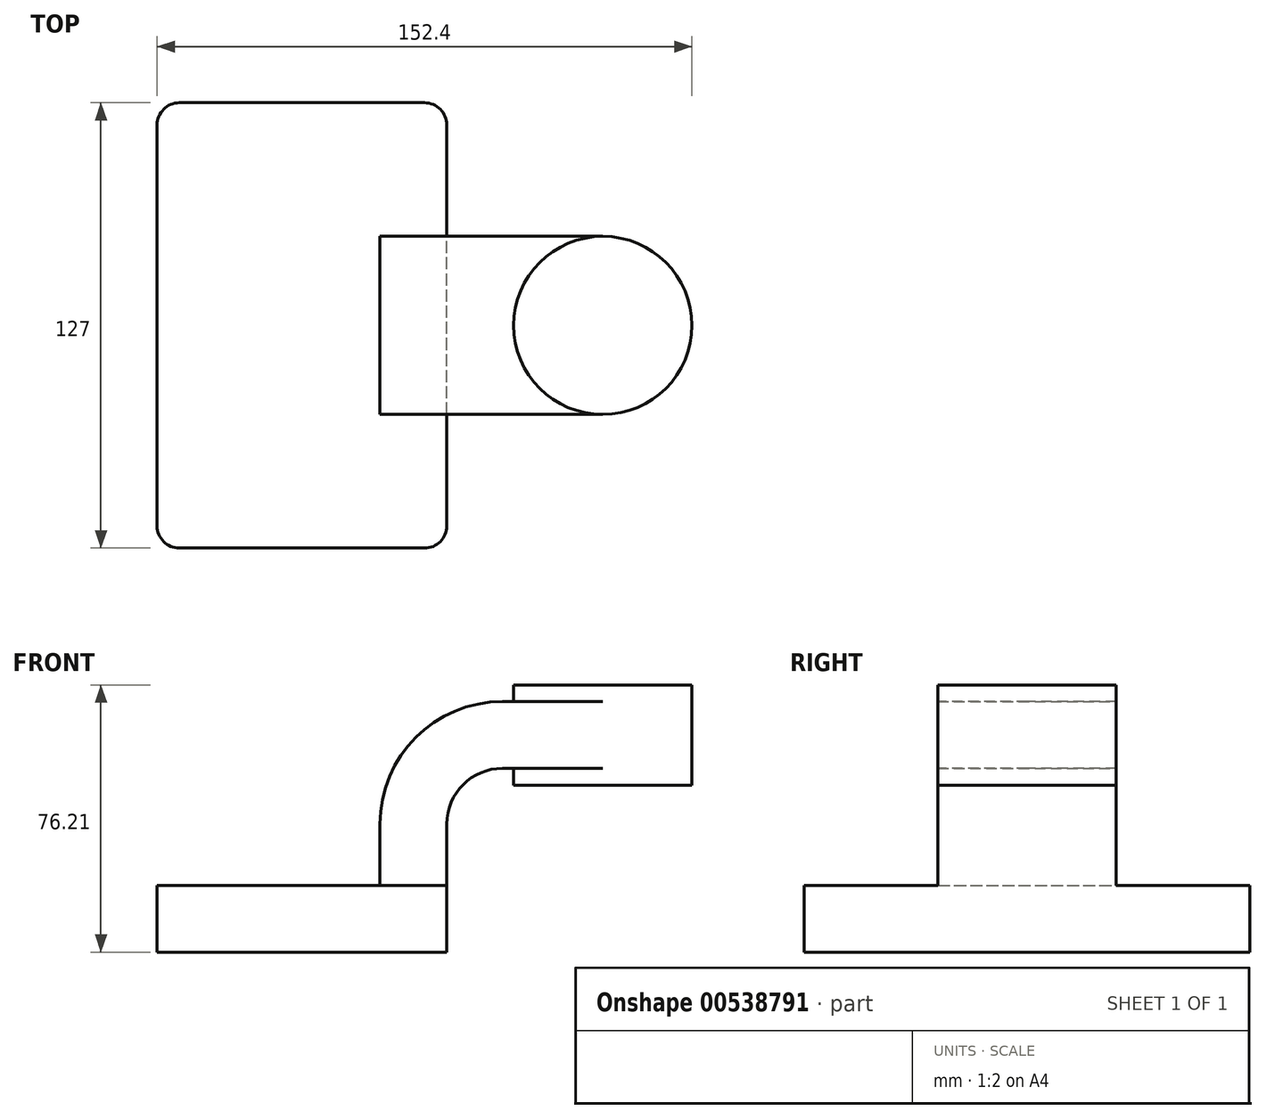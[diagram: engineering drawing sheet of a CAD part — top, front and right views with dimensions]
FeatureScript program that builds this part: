
annotation { "Feature Type Name" : "Feature", "Feature Type Description" : "" }
export const myFeature = defineFeature(function(context is Context, id is Id, definition is map)
    precondition{}
    {
        {
            var Q0;
            Q0=qCreatedBy(makeId("Front.planeOp"),FACE);
            var sketch = newSketch(context, id + "F0", { "sketchPlane" : qUnion([Q0])});
            skLineSegment(sketch, "E0.bottom", {"start": v(-41.27, -9.53) * mm, "end": v(41.28, -9.53) * mm});
            skLineSegment(sketch, "E0.top", {"start": v(-41.28, 9.53) * mm, "end": v(41.28, 9.53) * mm});
            skLineSegment(sketch, "E0.left", {"start": v(-41.28, -9.53) * mm, "end": v(-41.28, 9.53) * mm});
            skLineSegment(sketch, "E0.right", {"start": v(41.28, -9.53) * mm, "end": v(41.28, 9.53) * mm});
            skPoint(sketch, "E0.middle", {"position": v(0, 0) * mm});
            skLineSegment(sketch, "E1.bottom", {"start": v(60.32, 38.1) * mm, "end": v(111.12, 38.1) * mm});
            skLineSegment(sketch, "E1.top", {"start": v(60.32, 66.67) * mm, "end": v(111.12, 66.67) * mm});
            skLineSegment(sketch, "E1.left", {"start": v(60.32, 38.1) * mm, "end": v(60.32, 66.67) * mm});
            skLineSegment(sketch, "E1.right", {"start": v(111.12, 38.1) * mm, "end": v(111.12, 66.67) * mm});
            skPoint(sketch, "E1.middle", {"position": v(85.72, 52.39) * mm});
            skLineSegment(sketch, "E2", {"start": v(41.28, 9.53) * mm, "end": v(41.28, 27) * mm});
            skArc(sketch, "E3", {"start": v(41.27, 27) * mm, "mid": v(45.92, 38.23) * mm, "end": v(57.15, 42.88) * mm});
            skLineSegment(sketch, "E4", {"start": v(57.15, 42.88) * mm, "end": v(85.72, 42.88) * mm});
            skLineSegment(sketch, "E5.0", {"start": v(57.15, 61.93) * mm, "end": v(85.72, 61.93) * mm});
            skArc(sketch, "E5.1", {"start": v(22.23, 27) * mm, "mid": v(32.45, 51.7) * mm, "end": v(57.15, 61.93) * mm});
            skLineSegment(sketch, "E5.2", {"start": v(22.22, 9.53) * mm, "end": v(22.22, 27) * mm});
            skLineSegment(sketch, "E6", {"start": v(85.72, 38.1) * mm, "end": v(85.72, 66.67) * mm});
            skFitSpline(sketch, "E7", {"points": [v(-41.28, 9.53) * mm, v(57.15, 61.93) * mm], "startDerivative": vector(15.6, 107.84) * mm, "endDerivative": vector(95.92, -1.42) * mm});
            skSolve(sketch);
        }
        {
            var Q0;
            Q0=makeQuery(id+"F0.imprint","IMPRINT",FACE,{"disambiguationData":[TD([[makeQuery(id+"F0.imprint","IMPRINT",EDGE,{"derivedFrom":sQuery(id+"F0.wireOp",EDGE,"E0.bottom")}),1.0]])]});
            extrude(context, id + "F1", {"entities" : qUnion([Q0]), "endBound" : BoundingType.SYMMETRIC, "depth" : 127 * mm, "offsetDistance" : 25.4 * mm});
        }
        {
            var Q0;
            {var subQ1=sQuery(id+"F0.wireOp",EDGE,"E2");Q0=makeQuery(id+"F0.imprint","IMPRINT",FACE,{"disambiguationData":[TD([[makeQuery(id+"F0.imprint","IMPRINT",EDGE,{"derivedFrom":subQ1}),1.0]])]});}
            var Q1;
            {var subQ0=sQuery(id+"F0.wireOp",EDGE,"E4");var subQ1=sQuery(id+"F0.wireOp",EDGE,"E1.left");var subQ2=makeQuery(id+"F0.imprint","INTERSECT",VERTEX,{"derivedFrom":[subQ1,subQ0]});Q1=makeQuery(id+"F0.imprint","IMPRINT",FACE,{"disambiguationData":[TD([[makeQuery(id+"F0.imprint","IMPRINT",EDGE,{"disambiguationData":[TD([[subQ2,-1.0]])],"derivedFrom":subQ1}),-1.0]])]});}
            extrude(context, id + "F2", {"entities" : qUnion([Q0, Q1]), "operationType" : NewBodyOperationType.ADD, "endBound" : BoundingType.SYMMETRIC, "depth" : 50.8 * mm, "offsetDistance" : 25.4 * mm});
        }
        {
            var Q0;
            Q0=makeQuery(id+"F0.imprint","IMPRINT",FACE,{"disambiguationData":[TD([[makeQuery(id+"F0.imprint","IMPRINT",EDGE,{"derivedFrom":sQuery(id+"F0.wireOp",EDGE,"E5.1")}),1.0]])]});
            extrude(context, id + "F3", {"entities" : qUnion([Q0]), "operationType" : NewBodyOperationType.ADD, "endBound" : BoundingType.SYMMETRIC, "depth" : 15.88 * mm, "offsetDistance" : 25.4 * mm});
        }
        {
            var Q0;
            {var subQ0=sQuery(id+"F0.wireOp",EDGE,"E1.right");Q0=makeQuery(id+"F0.imprint","IMPRINT",FACE,{"disambiguationData":[TD([[makeQuery(id+"F0.imprint","IMPRINT",EDGE,{"derivedFrom":subQ0}),1.0]])]});}
            var Q1;
            Q1=sQuery(id+"F0.wireOp",EDGE,"E6");
            revolve(context, id + "F4", {"operationType" : NewBodyOperationType.ADD, "entities" : qUnion([Q0]), "axis" : qUnion([Q1]), "revolveType" : RevolveType.FULL});
        }
        {
            var Q0;
            Q0=makeQuery(id+"F1.opExtrude","CAP_EDGE",EDGE,{"disambiguationData":[OSD([sQuery(id+"F0.wireOp",EDGE,"E0.left")])],"isStart":false});
            var Q1;
            Q1=makeQuery(id+"F1.opExtrude","CAP_EDGE",EDGE,{"disambiguationData":[OSD([sQuery(id+"F0.wireOp",EDGE,"E0.right")])],"isStart":false});
            var Q2;
            Q2=makeQuery(id+"F1.opExtrude","CAP_EDGE",EDGE,{"disambiguationData":[OSD([sQuery(id+"F0.wireOp",EDGE,"E0.right")])],"isStart":true});
            var Q3;
            Q3=makeQuery(id+"F1.opExtrude","CAP_EDGE",EDGE,{"disambiguationData":[OSD([sQuery(id+"F0.wireOp",EDGE,"E0.left")])],"isStart":true});
            fillet(context, id + "F5", {"entities" : qUnion([Q0, Q1, Q2, Q3]), "radius" : 6.35 * mm, "tangentPropagation" : true, "allowEdgeOverflow" : false});
        }
    });
